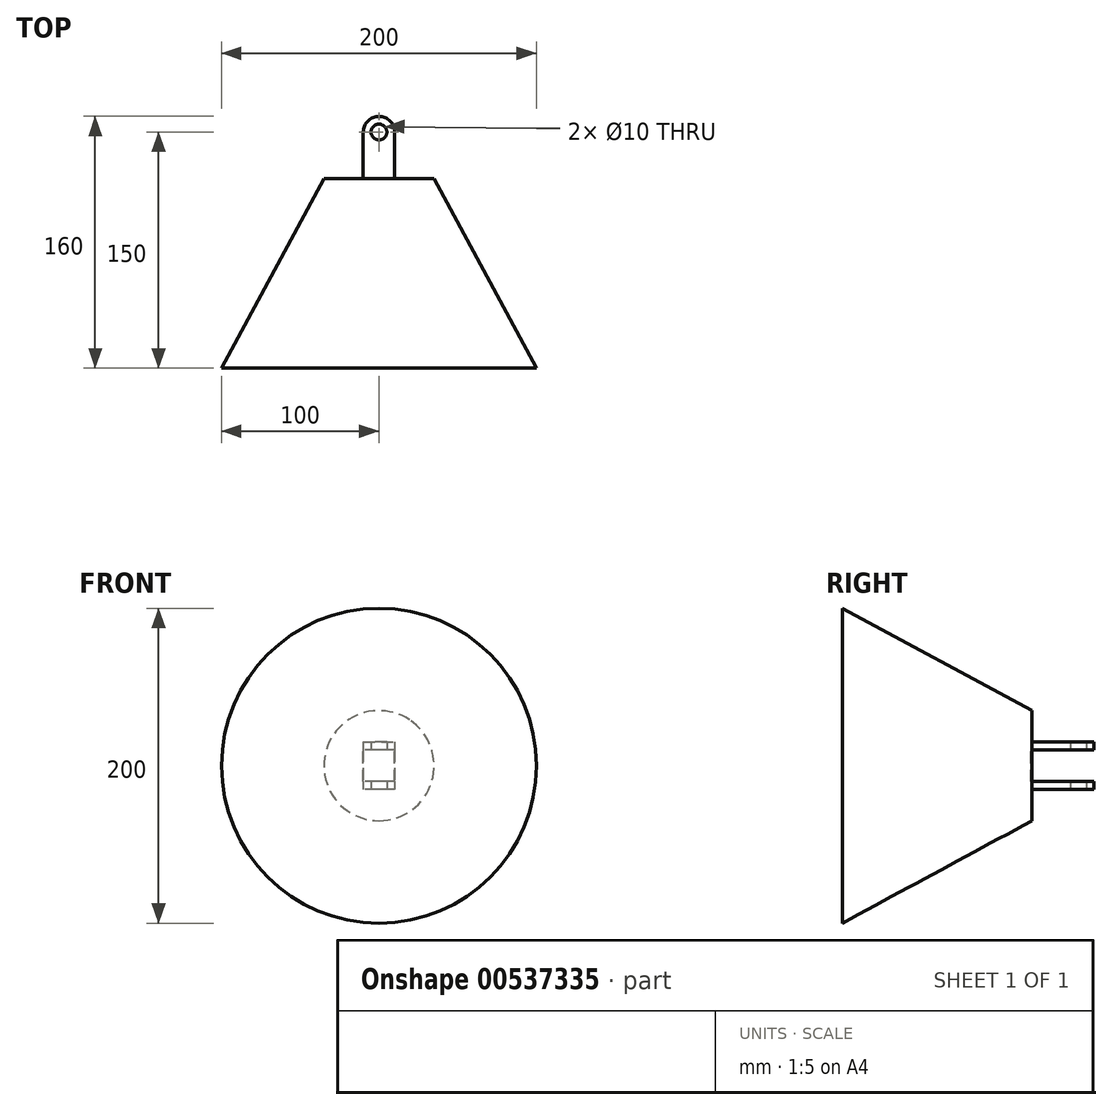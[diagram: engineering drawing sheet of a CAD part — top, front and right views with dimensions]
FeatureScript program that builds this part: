
annotation { "Feature Type Name" : "Feature", "Feature Type Description" : "" }
export const myFeature = defineFeature(function(context is Context, id is Id, definition is map)
    precondition{}
    {
        {
            var Q0;
            Q0=qCreatedBy(makeId("Top.planeOp"),FACE);
            var sketch = newSketch(context, id + "F0", { "sketchPlane" : qUnion([Q0])});
            skLineSegment(sketch, "E0", {"start": v(0, 0) * mm, "end": v(0, 120) * mm, "construction": true});
            skLineSegment(sketch, "E1", {"start": v(0, 0) * mm, "end": v(-100, 0) * mm});
            skLineSegment(sketch, "E2", {"start": v(-100, 0) * mm, "end": v(-35, 120.5) * mm});
            skLineSegment(sketch, "E3", {"start": v(-35, 120.5) * mm, "end": v(0, 120) * mm});
            skLineSegment(sketch, "E4", {"start": v(0, 0) * mm, "end": v(0, 120) * mm});
            skSolve(sketch);
        }
        {
            var Q0;
            Q0=makeQuery(id+"F0.imprint","IMPRINT",FACE,{"disambiguationData":[TD([[makeQuery(id+"F0.imprint","IMPRINT",EDGE,{"derivedFrom":sQuery(id+"F0.wireOp",EDGE,"E1")}),-1.0]])]});
            var Q1;
            Q1=sQuery(id+"F0.wireOp",EDGE,"E4");
            revolve(context, id + "F1", {"entities" : qUnion([Q0]), "axis" : qUnion([Q1]), "revolveType" : RevolveType.FULL});
        }
        {
            var Q0;
            Q0=qCreatedBy(makeId("Top.planeOp"),FACE);
            var sketch = newSketch(context, id + "F2", { "sketchPlane" : qUnion([Q0])});
            skLineSegment(sketch, "E5", {"start": v(0, 0) * mm, "end": v(0, 256.3) * mm, "construction": true});
            skLineSegment(sketch, "E6.top", {"start": v(0, 120) * mm, "end": v(-10, 120) * mm});
            skLineSegment(sketch, "E6.left", {"start": v(0, 150) * mm, "end": v(0, 120) * mm});
            skLineSegment(sketch, "E6.right", {"start": v(-10, 150) * mm, "end": v(-10, 120) * mm});
            skLineSegment(sketch, "E7.MirrorCS", {"start": v(10, 150) * mm, "end": v(10, 120) * mm});
            skArc(sketch, "E8", {"start": v(10, 150) * mm, "mid": v(0, 160) * mm, "end": v(-10, 150) * mm});
            skCircle(sketch, "E9", {"center": v(0, 150) * mm, "radius": 5 * mm});
            skPoint(sketch, "E10.MirrorCS.end.orphan", {"position": v(10, 150) * mm});
            skLineSegment(sketch, "E11", {"start": v(0, 120) * mm, "end": v(10, 120) * mm});
            skSolve(sketch);
        }
        {
            var Q0;
            Q0=qSketchRegion(id+"F2",true);
            extrude(context, id + "F3", {"entities" : qUnion([Q0]), "operationType" : NewBodyOperationType.ADD, "endBound" : BoundingType.SYMMETRIC, "depth" : 30 * mm});
        }
        {
            var Q0;
            Q0=qCreatedBy(makeId("Top.planeOp"),FACE);
            var sketch = newSketch(context, id + "F4", { "sketchPlane" : qUnion([Q0])});
            skLineSegment(sketch, "E12", {"start": v(0, 0) * mm, "end": v(0, 163.93) * mm, "construction": true});
            skLineSegment(sketch, "E13.bottom", {"start": v(0, 120) * mm, "end": v(-10, 120) * mm});
            skLineSegment(sketch, "E13.left", {"start": v(0, 120) * mm, "end": v(0, 150) * mm});
            skLineSegment(sketch, "E13.right", {"start": v(-10, 120) * mm, "end": v(-10, 150) * mm});
            skLineSegment(sketch, "E14.MirrorCS", {"start": v(10, 120) * mm, "end": v(10, 150) * mm});
            skLineSegment(sketch, "E15.MirrorCS", {"start": v(0, 120) * mm, "end": v(10, 120) * mm});
            skArc(sketch, "E16", {"start": v(10, 150) * mm, "mid": v(0, 160) * mm, "end": v(-10, 150) * mm});
            skCircle(sketch, "E17", {"center": v(0, 150) * mm, "radius": 5 * mm});
            skSolve(sketch);
        }
        {
            var Q0;
            Q0=qSketchRegion(id+"F4",true);
            extrude(context, id + "F5", {"entities" : qUnion([Q0]), "operationType" : NewBodyOperationType.REMOVE, "endBound" : BoundingType.SYMMETRIC, "oppositeDirection" : true, "depth" : 20 * mm});
        }
    });
